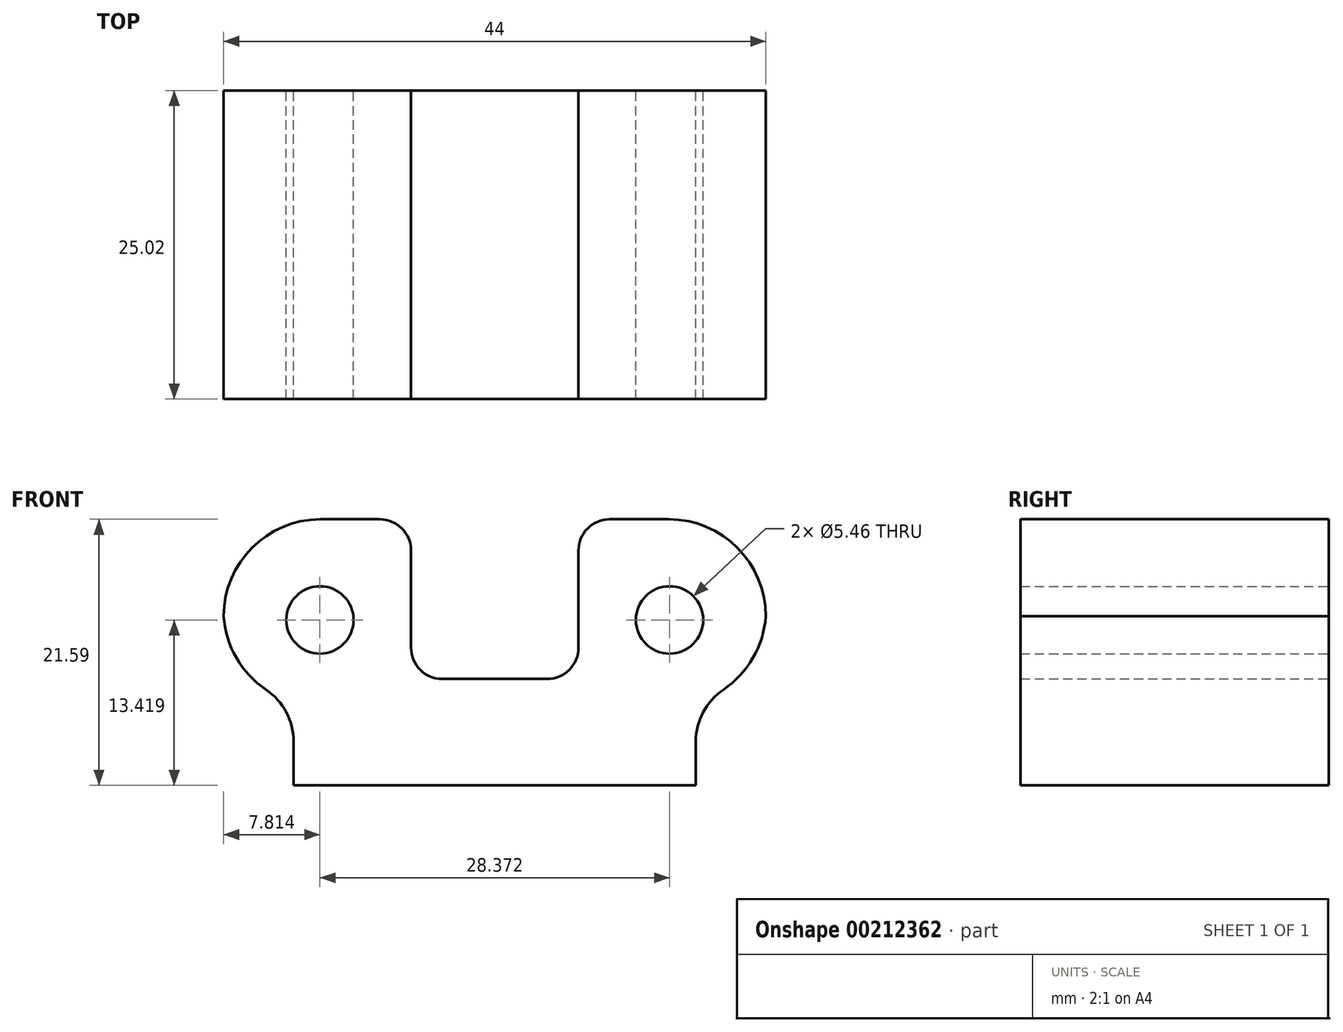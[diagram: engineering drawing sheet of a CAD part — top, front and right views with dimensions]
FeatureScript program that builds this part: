
annotation { "Feature Type Name" : "Feature", "Feature Type Description" : "" }
export const myFeature = defineFeature(function(context is Context, id is Id, definition is map)
    precondition{}
    {
        {
            var Q0;
            Q0=qCreatedBy(makeId("Front.planeOp"),FACE);
            var sketch = newSketch(context, id + "F0", { "sketchPlane" : qUnion([Q0])});
            skLineSegment(sketch, "E0.bottom", {"start": v(-22, 10.8) * mm, "end": v(-6.8, 10.8) * mm});
            skLineSegment(sketch, "E0.top", {"start": v(-16.32, -10.8) * mm, "end": v(0, -10.8) * mm});
            skLineSegment(sketch, "E0.left", {"start": v(-22, 10.8) * mm, "end": v(-22, -2.16) * mm});
            skPoint(sketch, "E1", {"position": v(0, 10.8) * mm});
            skPoint(sketch, "E2", {"position": v(-22, 0) * mm});
            skLineSegment(sketch, "E3.left", {"start": v(-16.32, -2.16) * mm, "end": v(-16.32, -10.8) * mm});
            skPoint(sketch, "E4", {"position": v(0, -10.8) * mm});
            skCircle(sketch, "E5", {"center": v(-14.19, 2.63) * mm, "radius": 2.73 * mm});
            skLineSegment(sketch, "E6.left", {"start": v(-6.8, 10.8) * mm, "end": v(-6.8, -2.16) * mm});
            skLineSegment(sketch, "E7", {"start": v(-16.32, -2.16) * mm, "end": v(-22, -2.16) * mm});
            skPoint(sketch, "E8.orphan", {"position": v(-22, -10.8) * mm});
            skLineSegment(sketch, "E9", {"start": v(-6.8, -2.16) * mm, "end": v(0, -2.16) * mm});
            skLineSegment(sketch, "E10", {"start": v(0, -10.8) * mm, "end": v(0, 10.8) * mm, "construction": true});
            skLineSegment(sketch, "E11.MirrorCS", {"start": v(6.8, -2.16) * mm, "end": v(0, -2.16) * mm});
            skLineSegment(sketch, "E12.MirrorCS", {"start": v(16.32, -10.8) * mm, "end": v(0, -10.8) * mm});
            skLineSegment(sketch, "E13.MirrorCS", {"start": v(16.32, -2.16) * mm, "end": v(22, -2.16) * mm});
            skLineSegment(sketch, "E14.MirrorCS", {"start": v(6.8, 10.8) * mm, "end": v(6.8, -2.16) * mm});
            skCircle(sketch, "E15.MirrorC", {"center": v(14.19, 2.63) * mm, "radius": 2.73 * mm});
            skLineSegment(sketch, "E16.MirrorCS", {"start": v(16.32, -2.16) * mm, "end": v(16.32, -10.8) * mm});
            skLineSegment(sketch, "E17.MirrorCS", {"start": v(22, 10.8) * mm, "end": v(22, -2.16) * mm});
            skLineSegment(sketch, "E18.MirrorCS", {"start": v(22, 10.8) * mm, "end": v(6.8, 10.8) * mm});
            skPoint(sketch, "E19.MirrorP", {"position": v(22, 0) * mm});
            skSolve(sketch);
        }
        {
            var Q0;
            Q0=makeQuery(id+"F0.imprint","IMPRINT",FACE,{"disambiguationData":[TD([[makeQuery(id+"F0.imprint","IMPRINT",EDGE,{"derivedFrom":sQuery(id+"F0.wireOp",EDGE,"E0.bottom")}),-1.0]])]});
            extrude(context, id + "F1", {"entities" : qUnion([Q0]), "depth" : 25.02 * mm});
        }
        {
            var Q0;
            Q0=makeQuery(id+"F1.opExtrude","SWEPT_EDGE",EDGE,{"disambiguationData":[OSD([sQuery(id+"F0.wireOp",EDGE,"E0.bottom"),sQuery(id+"F0.wireOp",EDGE,"E6.left")])]});
            var Q1;
            Q1=makeQuery(id+"F1.opExtrude","SWEPT_EDGE",EDGE,{"disambiguationData":[OSD([sQuery(id+"F0.wireOp",EDGE,"E6.left"),sQuery(id+"F0.wireOp",EDGE,"E9")])]});
            var Q2;
            Q2=makeQuery(id+"F1.opExtrude","SWEPT_EDGE",EDGE,{"disambiguationData":[OSD([sQuery(id+"F0.wireOp",EDGE,"E11.MirrorCS"),sQuery(id+"F0.wireOp",EDGE,"E14.MirrorCS")])]});
            var Q3;
            Q3=makeQuery(id+"F1.opExtrude","SWEPT_EDGE",EDGE,{"disambiguationData":[OSD([sQuery(id+"F0.wireOp",EDGE,"E14.MirrorCS"),sQuery(id+"F0.wireOp",EDGE,"E18.MirrorCS")])]});
            fillet(context, id + "F2", {"entities" : qUnion([Q0, Q1, Q2, Q3]), "radius" : 2.54 * mm, "tangentPropagation" : true, "allowEdgeOverflow" : false});
        }
        {
            var Q0;
            Q0=makeQuery(id+"F1.opExtrude","SWEPT_EDGE",EDGE,{"disambiguationData":[OSD([sQuery(id+"F0.wireOp",EDGE,"E0.bottom"),sQuery(id+"F0.wireOp",EDGE,"E0.left")])]});
            var Q1;
            Q1=makeQuery(id+"F1.opExtrude","SWEPT_EDGE",EDGE,{"disambiguationData":[OSD([sQuery(id+"F0.wireOp",EDGE,"E17.MirrorCS"),sQuery(id+"F0.wireOp",EDGE,"E18.MirrorCS")])]});
            fillet(context, id + "F3", {"entities" : qUnion([Q0, Q1]), "radius" : 7.87 * mm, "tangentPropagation" : true, "allowEdgeOverflow" : false});
        }
        {
            var Q0;
            Q0=makeQuery(id+"F1.opExtrude","SWEPT_EDGE",EDGE,{"disambiguationData":[OSD([sQuery(id+"F0.wireOp",EDGE,"E3.left"),sQuery(id+"F0.wireOp",EDGE,"E7")])]});
            var Q1;
            Q1=makeQuery(id+"F1.opExtrude","SWEPT_EDGE",EDGE,{"disambiguationData":[OSD([sQuery(id+"F0.wireOp",EDGE,"E13.MirrorCS"),sQuery(id+"F0.wireOp",EDGE,"E16.MirrorCS")])]});
            fillet(context, id + "F4", {"entities" : qUnion([Q0, Q1]), "radius" : 5.08 * mm, "tangentPropagation" : true, "allowEdgeOverflow" : false});
        }
        {
            var Q0;
            Q0=makeQuery(id+"F1.opExtrude","SWEPT_EDGE",EDGE,{"disambiguationData":[OSD([sQuery(id+"F0.wireOp",EDGE,"E0.left"),sQuery(id+"F0.wireOp",EDGE,"E7")])]});
            var Q1;
            Q1=makeQuery(id+"F1.opExtrude","SWEPT_EDGE",EDGE,{"disambiguationData":[OSD([sQuery(id+"F0.wireOp",EDGE,"E13.MirrorCS"),sQuery(id+"F0.wireOp",EDGE,"E17.MirrorCS")])]});
            fillet(context, id + "F5", {"entities" : qUnion([Q0, Q1]), "radius" : 7.87 * mm, "tangentPropagation" : true, "allowEdgeOverflow" : false});
        }
    });
